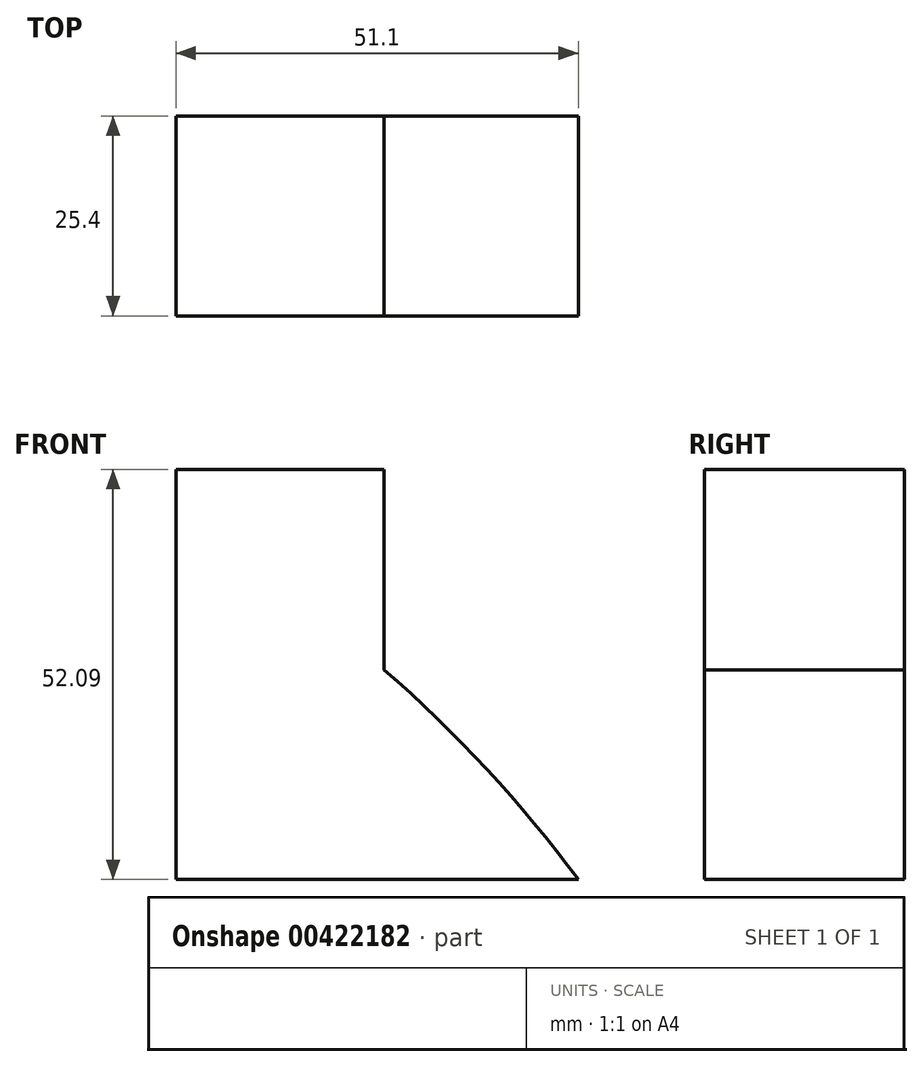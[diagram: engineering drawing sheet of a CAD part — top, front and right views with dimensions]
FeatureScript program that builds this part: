
annotation { "Feature Type Name" : "Feature", "Feature Type Description" : "" }
export const myFeature = defineFeature(function(context is Context, id is Id, definition is map)
    precondition{}
    {
        {
            var Q0;
            Q0=qCreatedBy(makeId("Front.planeOp"),FACE);
            var sketch = newSketch(context, id + "F0", { "sketchPlane" : qUnion([Q0])});
            skLineSegment(sketch, "E0", {"start": v(-60.08, 45.28) * mm, "end": v(-33.64, 45.28) * mm});
            skLineSegment(sketch, "E1", {"start": v(-60.08, 45.28) * mm, "end": v(-60.08, -6.8) * mm});
            skLineSegment(sketch, "E2", {"start": v(-60.08, -6.8) * mm, "end": v(-8.98, -6.8) * mm});
            skLineSegment(sketch, "E3", {"start": v(-33.64, 45.28) * mm, "end": v(-33.64, 19.83) * mm});
            skArc(sketch, "E4", {"start": v(-8.98, -6.8) * mm, "mid": v(-20.6, 7.17) * mm, "end": v(-33.64, 19.83) * mm});
            skSolve(sketch);
        }
        {
            var Q0;
            Q0=makeQuery(id+"F0.imprint","IMPRINT",FACE,{"disambiguationData":[TD([[makeQuery(id+"F0.imprint","IMPRINT",EDGE,{"derivedFrom":sQuery(id+"F0.wireOp",EDGE,"E0")}),-1.0]])]});
            extrude(context, id + "F1", {"entities" : qUnion([Q0]), "depth" : 25.4 * mm});
        }
    });
